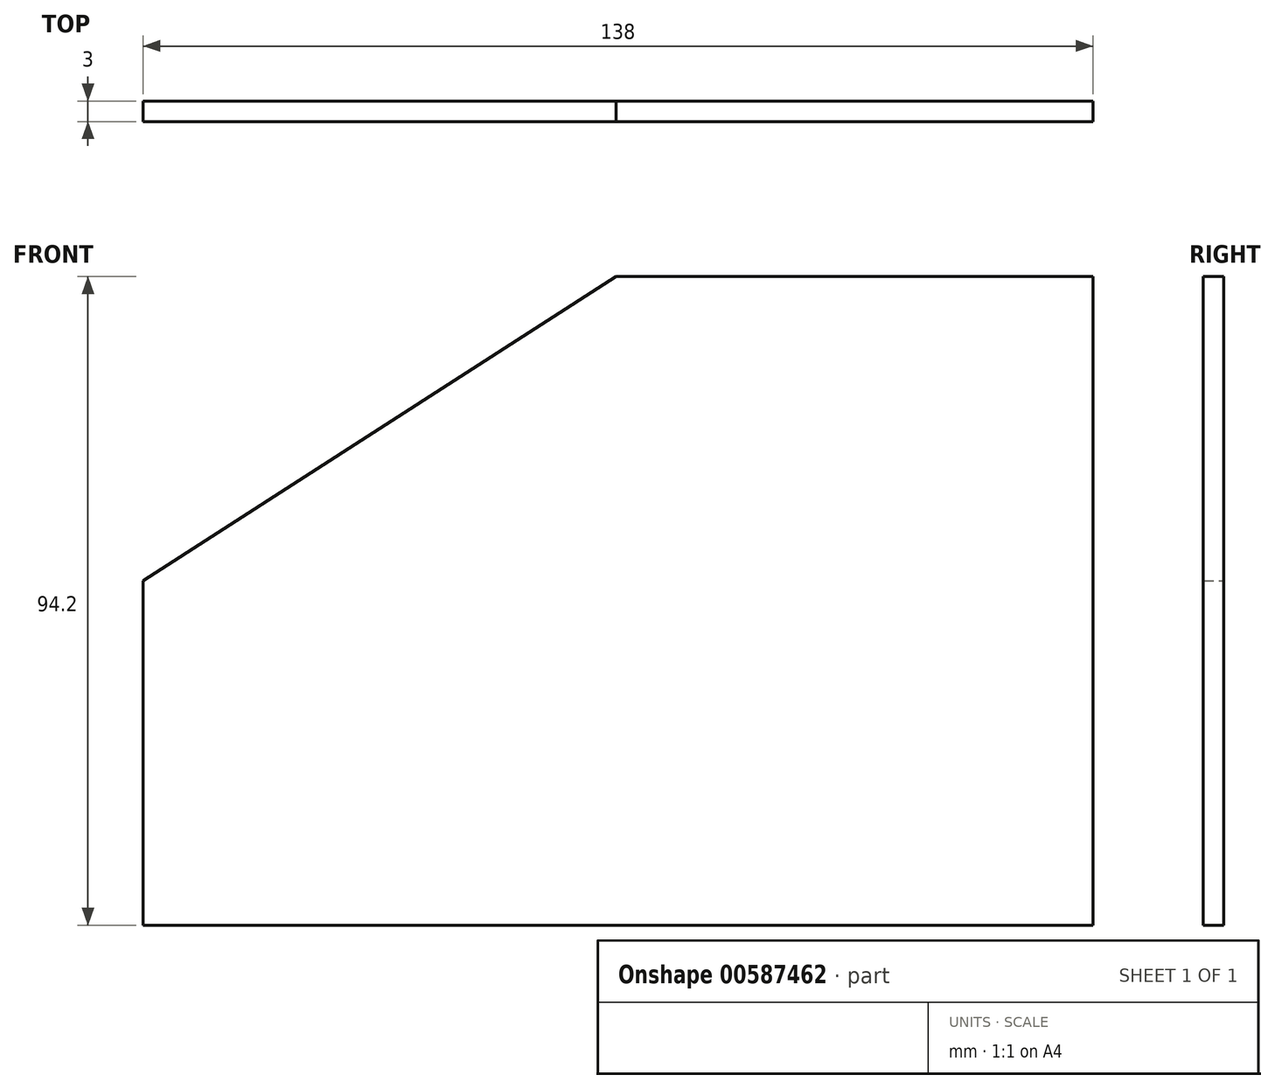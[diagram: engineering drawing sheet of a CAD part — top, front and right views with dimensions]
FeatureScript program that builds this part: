
annotation { "Feature Type Name" : "Feature", "Feature Type Description" : "" }
export const myFeature = defineFeature(function(context is Context, id is Id, definition is map)
    precondition{}
    {
        {
            var Q0;
            Q0=qCreatedBy(makeId("Front.planeOp"),FACE);
            var sketch = newSketch(context, id + "F0", { "sketchPlane" : qUnion([Q0])});
            skLineSegment(sketch, "E0", {"start": v(29.34, 44.2) * mm, "end": v(98.62, 44.2) * mm});
            skLineSegment(sketch, "E1", {"start": v(98.62, 44.2) * mm, "end": v(98.62, -50) * mm});
            skLineSegment(sketch, "E2", {"start": v(98.62, -50) * mm, "end": v(-39.38, -50) * mm});
            skLineSegment(sketch, "E3", {"start": v(-39.38, -50) * mm, "end": v(-39.38, 0) * mm});
            skLineSegment(sketch, "E4", {"start": v(-39.38, 0) * mm, "end": v(29.34, 44.2) * mm});
            skSolve(sketch);
        }
        {
            var Q0;
            Q0 = qSketchRegion(id + "F0", true);
            extrude(context, id + "F1", {"entities" : qUnion([Q0]), "depth" : 3 * mm, "offsetDistance" : 25 * mm});
        }
    });
